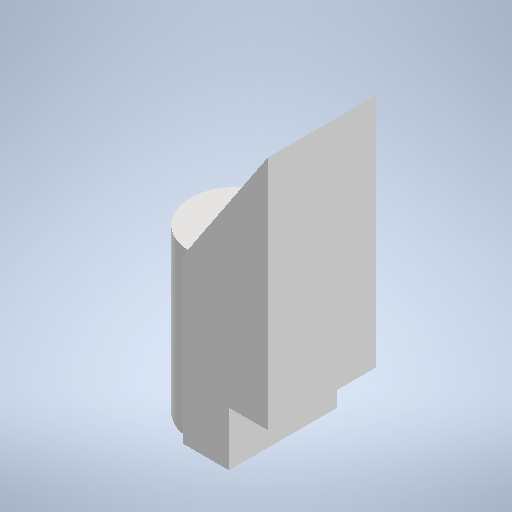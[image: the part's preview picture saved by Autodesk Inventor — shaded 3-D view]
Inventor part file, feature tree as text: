
AUTODESK INVENTOR PART (.ipt)
format: ipt  version: 2025 (Build 290162000, 162)  size: 271,360 bytes
history: native  units: mm
features: extrude x7, sketch x2
ambient origin geometry x8: Origin, YZ Plane, XZ Plane, XY Plane, X Axis, Y Axis, Z Axis, Center Point
bodies: Body1 (feature_tree)
feature tree (9):
  sketch  "Szkic1"
  extrude  "Wyciągnięcie proste4"  Depth=8.0mm
  extrude  "Wyciągnięcie proste5"  Depth=14.0mm
  extrude  "Wyciągnięcie proste6"  Depth=11.0mm
  extrude  "Wyciągnięcie proste7"  Depth=7.0mm
  extrude  "Wyciągnięcie proste8"  TaperAngle=0.0deg  [1 undecoded]
  extrude  "Wyciągnięcie proste9"  Depth=5.0mm
  extrude  "Wyciągnięcie proste10"  Depth=12.0mm
  sketch  "Szkic5"
note: 1 required parameter value undecoded (feature->parameter linkage not recoverable at this tier; creation-order binding heuristic only, values carry confidence <= 0.55)
